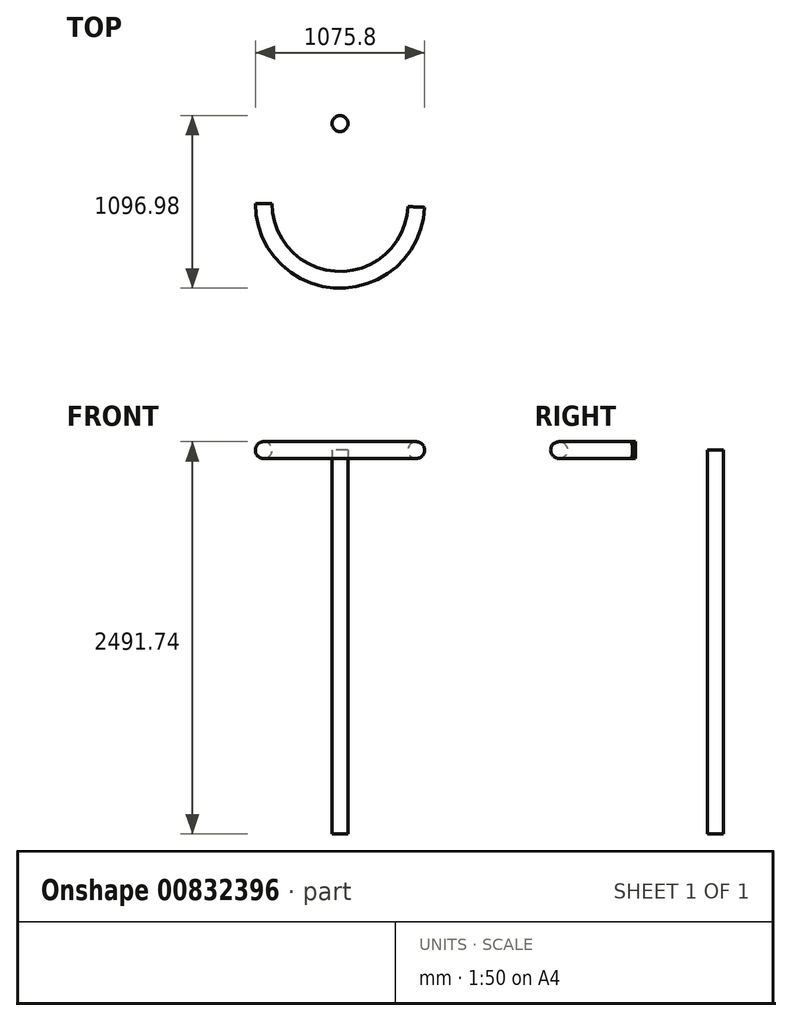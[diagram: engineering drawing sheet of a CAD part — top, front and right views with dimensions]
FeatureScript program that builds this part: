
annotation { "Feature Type Name" : "Feature", "Feature Type Description" : "" }
export const myFeature = defineFeature(function(context is Context, id is Id, definition is map)
    precondition{}
    {
        {
            var Q0;
            Q0=qCreatedBy(makeId("Top.planeOp"),FACE);
            var sketch = newSketch(context, id + "F0", { "sketchPlane" : qUnion([Q0])});
            skCircle(sketch, "E0", {"center": v(0, 0) * mm, "radius": 50.8 * mm});
            skSolve(sketch);
        }
        {
            var Q0;
            Q0 = qSketchRegion(id + "F0", true);
            extrude(context, id + "F1", {"entities" : qUnion([Q0]), "depth" : 2438.4 * mm, "offsetDistance" : 25.4 * mm});
        }
        {
            var Q0;
            Q0=qCreatedBy(makeId("Right.planeOp"),FACE);
            var sketch = newSketch(context, id + "F2", { "sketchPlane" : qUnion([Q0])});
            skLineSegment(sketch, "E1", {"start": v(0, 0) * mm, "end": v(0, 2438.4) * mm});
            skLineSegment(sketch, "E2", {"start": v(0, 2438.4) * mm, "end": v(-508, 2438.4) * mm});
            skSolve(sketch);
        }
        {
            var Q0;
            Q0=sQuery(id+"F2.wireOp",VERTEX,"E1.end");
            var Q1;
            Q1=sQuery(id+"F2.wireOp",EDGE,"E1");
            cPlane(context, id + "F3", {"entities" : qUnion([Q0, Q1]), "cplaneType" : CPlaneType.LINE_POINT, "offset" : 25.4 * mm, "width" : 152.4 * mm, "height" : 152.4 * mm});
        }
        {
            var Q0;
            Q0=qCreatedBy(id+"F3.planeOp",FACE);
            var sketch = newSketch(context, id + "F4", { "sketchPlane" : qUnion([Q0])});
            skLineSegment(sketch, "E3", {"start": v(0, 0) * mm, "end": v(0, -508) * mm});
            skArc(sketch, "E4", {"start": v(-507.47, -484.84) * mm, "mid": v(11.58, -0.13) * mm, "end": v(508, -508) * mm});
            skSolve(sketch);
        }
        {
            var Q0;
            Q0=sQuery(id+"F4.wireOp",VERTEX,"E4.start");
            var Q1;
            Q1=sQuery(id+"F4.wireOp",EDGE,"E4");
            cPlane(context, id + "F5", {"entities" : qUnion([Q0, Q1]), "cplaneType" : CPlaneType.CURVE_POINT, "offset" : 25.4 * mm, "width" : 152.4 * mm, "height" : 152.4 * mm});
        }
        {
            var Q0;
            Q0=qCreatedBy(id+"F5.planeOp",FACE);
            var sketch = newSketch(context, id + "F6", { "sketchPlane" : qUnion([Q0])});
            skCircle(sketch, "E5", {"center": v(484.84, 2438.4) * mm, "radius": 53.34 * mm});
            skSolve(sketch);
        }
        {
            var Q0;
            Q0=makeQuery(id+"F6.imprint","IMPRINT",FACE,{"disambiguationData":[TD([[makeQuery(id+"F6.imprint","IMPRINT",EDGE,{"derivedFrom":sQuery(id+"F6.wireOp",EDGE,"E5")}),1.0]])]});
            var Q1;
            Q1=sQuery(id+"F6.wireOp",EDGE,"E5");
            var Q2;
            Q2=sQuery(id+"F4.wireOp",EDGE,"E4");
            sweep(context, id + "F7", {"operationType" : NewBodyOperationType.ADD, "profiles" : qUnion([Q0]), "surfaceProfiles" : qUnion([Q1]), "path" : qUnion([Q2])});
        }
    });
